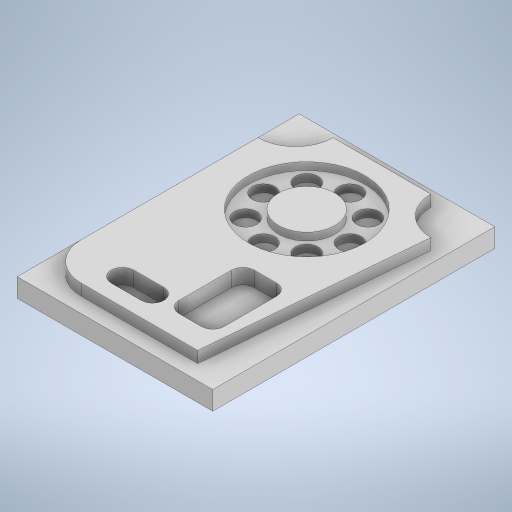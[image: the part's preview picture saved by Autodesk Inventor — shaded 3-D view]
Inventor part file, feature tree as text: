
AUTODESK INVENTOR PART (.ipt)
format: ipt  version: 2023.2 (Build 272271000, 271)  size: 342,016 bytes
history: native  units: mm
features: extrude x4, sketch x4
ambient origin geometry x8: Origin, YZ Plane, XZ Plane, XY Plane, X Axis, Y Axis, Z Axis, Center Point
bodies: Solid1 (feature_tree)
feature tree (8):
  extrude  "Extrusion1"  Depth=75.0mm
  extrude  "Extrusion2"  Depth=4.0mm
  extrude  "Extrusion3"  Depth=20.0mm
  extrude  "Extrusion4"  Depth=20.0mm
  sketch  "Sketch1"  dims[d0=52.0mm d1=75.0mm]
  sketch  "Sketch2"  dims[d2=5.0mm d3=0.0mm d4=4.0mm]
  sketch  "Sketch3"  dims[d5=3.0mm d6=20.0mm]
  sketch  "Sketch4"  dims[d7=4.0mm d8=20.0mm d9=4.0mm d10=3.0mm d11=8.0mm d12=3.0mm d13=10.0mm d14=3.0mm d15=0.0mm d16=22.0mm d17=30.0mm d18=20.0mm d19=12.0mm d20=3.0mm d21=6.0mm d22=6.0mm d23=27.0mm d24=11.0mm d25=11.0mm d26=35.0mm d27=15.0mm d28=51.0mm d29=26.0mm d30=6.0mm d31=11.5mm d32=80.0mm d34=360.0deg d36=4.0mm d37=0.0mm d38=15.0mm d39=26.0mm d40=51.0mm d41=31.0mm d42=2.0mm d43=0.0mm]
